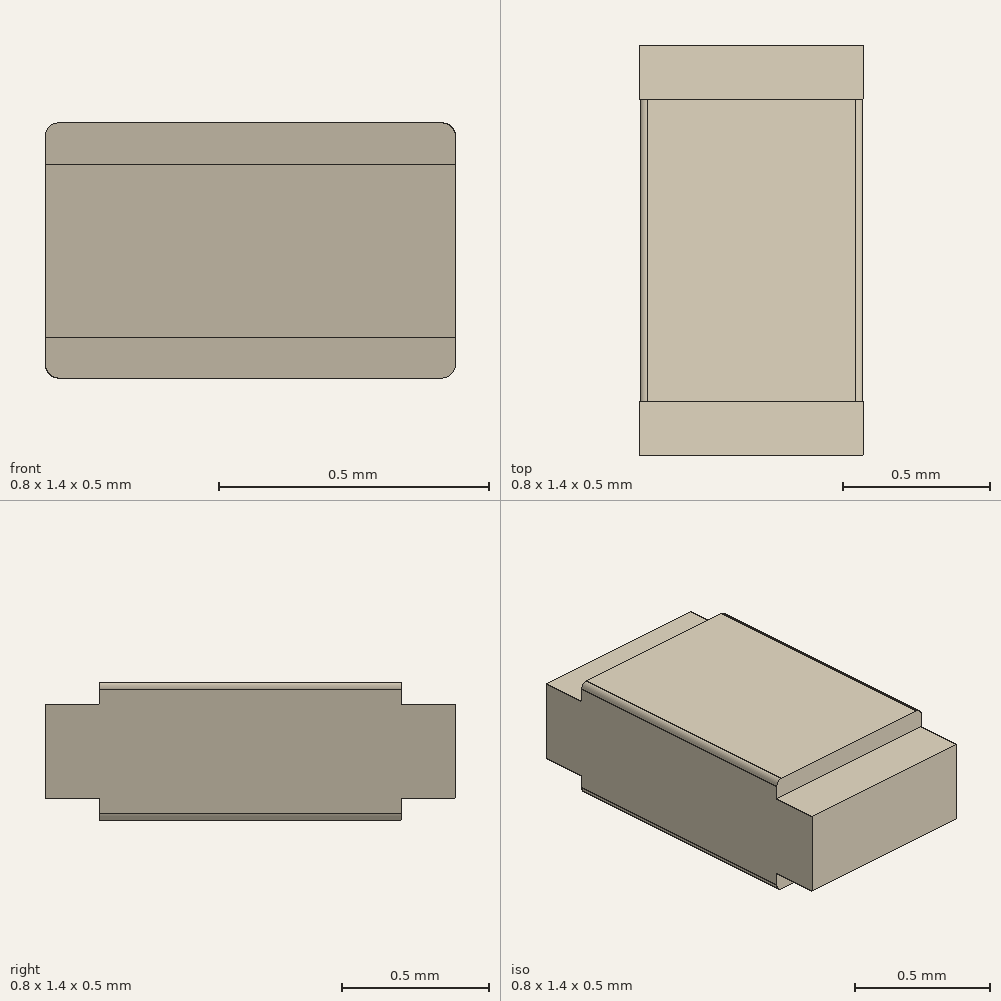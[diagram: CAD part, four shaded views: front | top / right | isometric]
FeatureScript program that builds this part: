
annotation { "Feature Type Name" : "Feature", "Feature Type Description" : "" }
export const myFeature = defineFeature(function(context is Context, id is Id, definition is map)
    precondition{}
    {
        {
            var Q0;
            Q0=qCreatedBy(makeId("Right.planeOp"),FACE);
            var sketch = newSketch(context, id + "F0", { "sketchPlane" : qUnion([Q0])});
            skLineSegment(sketch, "E0.rect.bottom", {"start": v(0.8, 0.25) * mm, "end": v(-0.8, 0.25) * mm});
            skLineSegment(sketch, "E0.rect.top", {"start": v(0.8, -0.25) * mm, "end": v(-0.8, -0.25) * mm});
            skLineSegment(sketch, "E0.rect.left", {"start": v(0.8, 0.25) * mm, "end": v(0.8, -0.25) * mm});
            skLineSegment(sketch, "E0.rect.right", {"start": v(-0.8, 0.25) * mm, "end": v(-0.8, -0.25) * mm});
            skPoint(sketch, "E0.rect.middle", {"position": v(0, 0) * mm});
            skLineSegment(sketch, "E1", {"start": v(-0.51, 0.25) * mm, "end": v(-0.51, 0.16) * mm});
            skLineSegment(sketch, "E2", {"start": v(-0.51, 0.16) * mm, "end": v(-0.7, 0.16) * mm});
            skLineSegment(sketch, "E3", {"start": v(-0.7, 0.16) * mm, "end": v(-0.7, -0.16) * mm});
            skLineSegment(sketch, "E4", {"start": v(-0.7, -0.16) * mm, "end": v(-0.51, -0.16) * mm});
            skLineSegment(sketch, "E5", {"start": v(-0.51, -0.16) * mm, "end": v(-0.51, -0.25) * mm});
            skLineSegment(sketch, "E6.MirrorCS", {"start": v(0.51, 0.25) * mm, "end": v(0.51, 0.16) * mm});
            skLineSegment(sketch, "E7.MirrorCS", {"start": v(0.51, 0.16) * mm, "end": v(0.7, 0.16) * mm});
            skLineSegment(sketch, "E8.MirrorCS", {"start": v(0.7, 0.16) * mm, "end": v(0.7, -0.16) * mm});
            skLineSegment(sketch, "E9.MirrorCS", {"start": v(0.7, -0.16) * mm, "end": v(0.51, -0.16) * mm});
            skLineSegment(sketch, "E10.MirrorCS", {"start": v(0.51, -0.16) * mm, "end": v(0.51, -0.25) * mm});
            skLineSegment(sketch, "E11.bottom", {"start": v(0.51, 0.24) * mm, "end": v(-0.51, 0.24) * mm});
            skLineSegment(sketch, "E11.top", {"start": v(0.51, -0.24) * mm, "end": v(-0.51, -0.24) * mm});
            skLineSegment(sketch, "E11.left", {"start": v(0.51, 0.24) * mm, "end": v(0.51, -0.24) * mm});
            skLineSegment(sketch, "E11.right", {"start": v(-0.51, 0.24) * mm, "end": v(-0.51, -0.24) * mm});
            skSolve(sketch);
        }
        {
            var Q0;
            {var subQ4=sQuery(id+"F0.wireOp",EDGE,"E11.bottom");Q0=makeQuery(id+"F0.imprint","IMPRINT",FACE,{"disambiguationData":[TD([[makeQuery(id+"F0.imprint","IMPRINT",EDGE,{"derivedFrom":subQ4}),1.0]])]});}
            var Q1;
            {var subQ2=sQuery(id+"F0.wireOp",EDGE,"E2");Q1=makeQuery(id+"F0.imprint","IMPRINT",FACE,{"disambiguationData":[TD([[makeQuery(id+"F0.imprint","IMPRINT",EDGE,{"derivedFrom":subQ2}),1.0]])]});}
            var Q2;
            {var subQ2=sQuery(id+"F0.wireOp",EDGE,"E7.MirrorCS");Q2=makeQuery(id+"F0.imprint","IMPRINT",FACE,{"disambiguationData":[TD([[makeQuery(id+"F0.imprint","IMPRINT",EDGE,{"derivedFrom":subQ2}),-1.0]])]});}
            extrude(context, id + "F1", {"entities" : qUnion([Q0, Q1, Q2]), "endBound" : BoundingType.SYMMETRIC, "depth" : 0.76 * mm});
        }
        {
            var Q0;
            Q0=makeQuery(id+"F1.opExtrude","CAP_EDGE",EDGE,{"disambiguationData":[OSD([sQuery(id+"F0.wireOp",EDGE,"E11.bottom")])],"isStart":true});
            var Q1;
            Q1=makeQuery(id+"F1.opExtrude","CAP_EDGE",EDGE,{"disambiguationData":[OSD([sQuery(id+"F0.wireOp",EDGE,"E11.bottom")])],"isStart":false});
            var Q2;
            Q2=makeQuery(id+"F1.opExtrude","CAP_EDGE",EDGE,{"disambiguationData":[OSD([sQuery(id+"F0.wireOp",EDGE,"E11.top")])],"isStart":false});
            var Q3;
            Q3=makeQuery(id+"F1.opExtrude","CAP_EDGE",EDGE,{"disambiguationData":[OSD([sQuery(id+"F0.wireOp",EDGE,"E11.top")])],"isStart":true});
            fillet(context, id + "F2", {"entities" : qUnion([Q0, Q1, Q2, Q3]), "radius" : 0.03 * mm, "allowEdgeOverflow" : false});
        }
    });
